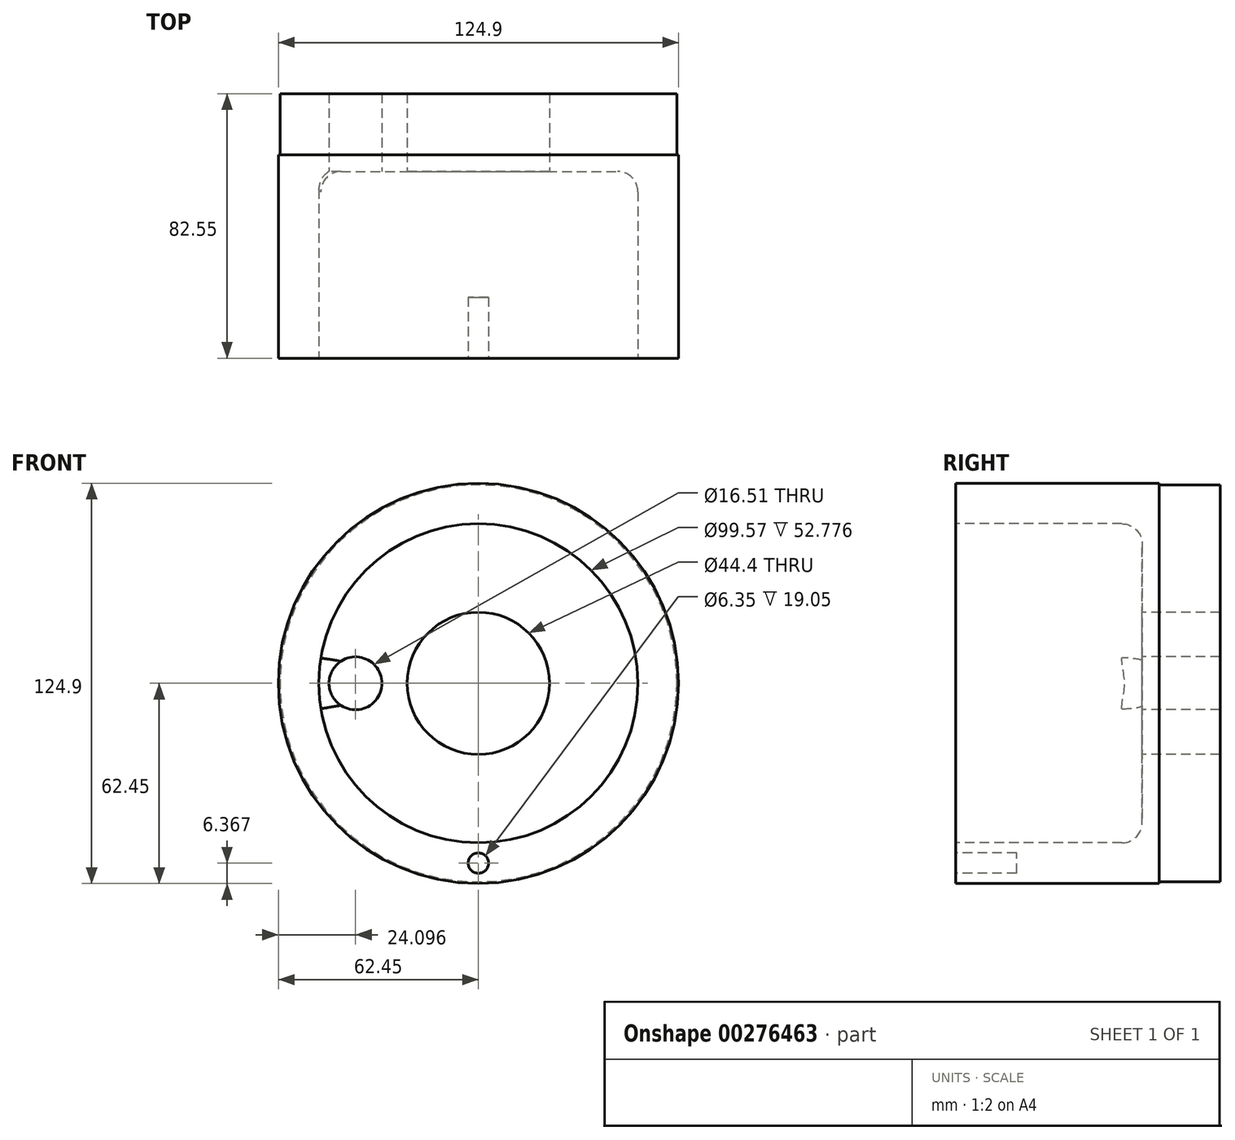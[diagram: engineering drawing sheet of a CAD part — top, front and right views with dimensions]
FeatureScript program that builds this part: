
annotation { "Feature Type Name" : "Feature", "Feature Type Description" : "" }
export const myFeature = defineFeature(function(context is Context, id is Id, definition is map)
    precondition{}
    {
        {
            var Q0;
            Q0=qCreatedBy(makeId("Front.planeOp"),FACE);
            var sketch = newSketch(context, id + "F0", { "sketchPlane" : qUnion([Q0])});
            skCircle(sketch, "E0", {"center": v(0, 0) * mm, "radius": 62.45 * mm});
            skSolve(sketch);
        }
        {
            var Q0;
            Q0=makeQuery(id+"F0.imprint","IMPRINT",FACE,{"disambiguationData":[TD([[makeQuery(id+"F0.imprint","IMPRINT",EDGE,{"derivedFrom":sQuery(id+"F0.wireOp",EDGE,"E0")}),1.0]])]});
            extrude(context, id + "F1", {"entities" : qUnion([Q0]), "depth" : 63.5 * mm});
        }
        {
            var Q0;
            Q0=makeQuery(id+"F1.opExtrude","CAP_FACE",FACE,{"disambiguationData":[OSD([sQuery(id+"F0.wireOp",EDGE,"E0")])],"isStart":true});
            var sketch = newSketch(context, id + "F2", { "sketchPlane" : qUnion([Q0])});
            skCircle(sketch, "E1", {"center": v(0, 0) * mm, "radius": 61.93 * mm});
            skSolve(sketch);
        }
        {
            var Q0;
            Q0=makeQuery(id+"F2.imprint","IMPRINT",FACE,{"disambiguationData":[TD([[makeQuery(id+"F2.imprint","IMPRINT",EDGE,{"derivedFrom":sQuery(id+"F2.wireOp",EDGE,"E1")}),1.0]])]});
            extrude(context, id + "F3", {"entities" : qUnion([Q0]), "operationType" : NewBodyOperationType.ADD, "offsetDistance" : 25.4 * mm, "depth" : 19.05 * mm});
        }
        {
            var Q0;
            Q0=makeQuery(id+"F1.opExtrude","CAP_FACE",FACE,{"disambiguationData":[OSD([sQuery(id+"F0.wireOp",EDGE,"E0")])],"isStart":false});
            var sketch = newSketch(context, id + "F4", { "sketchPlane" : qUnion([Q0])});
            skCircle(sketch, "E2", {"center": v(-38.35, 0) * mm, "radius": 8.26 * mm});
            skLineSegment(sketch, "E3", {"start": v(-38.35, 0) * mm, "end": v(0, 0) * mm});
            skSolve(sketch);
        }
        {
            var Q0;
            Q0=makeQuery(id+"F4.imprint","IMPRINT",FACE,{"disambiguationData":[TD([[makeQuery(id+"F4.imprint","IMPRINT",EDGE,{"derivedFrom":sQuery(id+"F4.wireOp",EDGE,"E2")}),1.0]])]});
            extrude(context, id + "F5", {"entities" : qUnion([Q0]), "operationType" : NewBodyOperationType.REMOVE, "endBound" : BoundingType.THROUGH_ALL, "oppositeDirection" : true, "depth" : 25.4 * mm});
        }
        {
            var Q0;
            Q0=makeQuery(id+"F1.opExtrude","CAP_FACE",FACE,{"disambiguationData":[OSD([sQuery(id+"F0.wireOp",EDGE,"E0")])],"isStart":false});
            var sketch = newSketch(context, id + "F6", { "sketchPlane" : qUnion([Q0])});
            skCircle(sketch, "E4", {"center": v(0, 0) * mm, "radius": 49.78 * mm});
            skSolve(sketch);
        }
        {
            var Q0;
            Q0=makeQuery(id+"F6.imprint","IMPRINT",FACE,{"disambiguationData":[TD([[makeQuery(id+"F6.imprint","IMPRINT",EDGE,{"derivedFrom":sQuery(id+"F6.wireOp",EDGE,"E4")}),1.0]])]});
            extrude(context, id + "F7", {"entities" : qUnion([Q0]), "operationType" : NewBodyOperationType.REMOVE, "oppositeDirection" : true, "depth" : 58.27 * mm});
        }
        {
            var Q0;
            Q0=makeQuery(id+"F7.boolean.opBoolean","COPY",EDGE,{"derivedFrom":makeQuery(id+"F7.opExtrude","CAP_EDGE",EDGE,{"disambiguationData":[OSD([sQuery(id+"F6.wireOp",EDGE,"E4")])],"isStart":false})});
            fillet(context, id + "F8", {"entities" : qUnion([Q0]), "radius" : 6.35 * mm, "tangentPropagation" : true, "allowEdgeOverflow" : false});
        }
        {
            var Q0;
            Q0=makeQuery(id+"F7.boolean.opBoolean","COPY",FACE,{"derivedFrom":makeQuery(id+"F7.opExtrude","CAP_FACE",FACE,{"disambiguationData":[OSD([sQuery(id+"F4.wireOp",EDGE,"E2"),sQuery(id+"F6.wireOp",EDGE,"E4")])],"isStart":false})});
            var sketch = newSketch(context, id + "F9", { "sketchPlane" : qUnion([Q0])});
            skCircle(sketch, "E5", {"center": v(0, 0) * mm, "radius": 22.2 * mm});
            skCircle(sketch, "E6", {"center": v(0, 0) * mm, "radius": 26.99 * mm});
            skSolve(sketch);
        }
        {
            var Q0;
            Q0=makeQuery(id+"F9.imprint","IMPRINT",FACE,{"disambiguationData":[TD([[makeQuery(id+"F9.imprint","IMPRINT",EDGE,{"derivedFrom":sQuery(id+"F9.wireOp",EDGE,"E5")}),1.0]])]});
            extrude(context, id + "F10", {"entities" : qUnion([Q0]), "operationType" : NewBodyOperationType.REMOVE, "endBound" : BoundingType.THROUGH_ALL, "oppositeDirection" : true, "depth" : 25.4 * mm});
        }
        {
            var Q0;
            Q0=makeQuery(id+"F1.opExtrude","CAP_FACE",FACE,{"disambiguationData":[OSD([sQuery(id+"F0.wireOp",EDGE,"E0")])],"isStart":false});
            var sketch = newSketch(context, id + "F11", { "sketchPlane" : qUnion([Q0])});
            skCircle(sketch, "E7", {"center": v(0, 0) * mm, "radius": 56.08 * mm});
            skLineSegment(sketch, "E8", {"start": v(0, 0) * mm, "end": v(0, -56.08) * mm});
            skCircle(sketch, "E9", {"center": v(0, -56.08) * mm, "radius": 3.18 * mm});
            skSolve(sketch);
        }
        {
            var Q0;
            {var subQ0=sQuery(id+"F11.wireOp",EDGE,"E7");var subQ1=makeQuery(id+"F11.imprint","INTERSECT",VERTEX,{"derivedFrom":[subQ0,sQuery(id+"F11.wireOp",EDGE,"E8")]});Q0=makeQuery(id+"F11.imprint","IMPRINT",FACE,{"disambiguationData":[TD([[makeQuery(id+"F11.imprint","IMPRINT",EDGE,{"disambiguationData":[TD([[subQ1,1.0]])],"derivedFrom":subQ0}),-1.0]])]});}
            var Q1;
            {var subQ0=sQuery(id+"F11.wireOp",EDGE,"E8");var subQ1=sQuery(id+"F11.wireOp",EDGE,"E7");var subQ2=makeQuery(id+"F11.imprint","INTERSECT",VERTEX,{"derivedFrom":[subQ1,subQ0]});Q1=makeQuery(id+"F11.imprint","IMPRINT",FACE,{"disambiguationData":[TD([[makeQuery(id+"F11.imprint","IMPRINT",EDGE,{"disambiguationData":[TD([[subQ2,1.0]])],"derivedFrom":subQ1}),1.0]])]});}
            var Q2;
            {var subQ0=sQuery(id+"F11.wireOp",EDGE,"E8");var subQ1=sQuery(id+"F11.wireOp",EDGE,"E7");var subQ2=makeQuery(id+"F11.imprint","INTERSECT",VERTEX,{"derivedFrom":[subQ1,subQ0]});Q2=makeQuery(id+"F11.imprint","IMPRINT",FACE,{"disambiguationData":[TD([[makeQuery(id+"F11.imprint","IMPRINT",EDGE,{"disambiguationData":[TD([[subQ2,-1.0]])],"derivedFrom":subQ1}),1.0]])]});}
            extrude(context, id + "F12", {"entities" : qUnion([Q0, Q1, Q2]), "operationType" : NewBodyOperationType.REMOVE, "oppositeDirection" : true, "depth" : 19.05 * mm});
        }
    });
